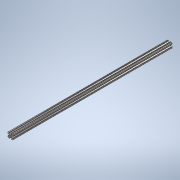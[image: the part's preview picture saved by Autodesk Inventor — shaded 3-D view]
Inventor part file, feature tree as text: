
AUTODESK INVENTOR PART (.ipt)
format: ipt  version: 2020 (Build 240168000, 168)  size: 244,224 bytes
history: native  units: in
note: dims shown in document units (in); Inventor stores cm internally (conversion verified against a paired STEP export)
features: extrude x1, sketch x1
ambient origin geometry x8: Origin, YZ Plane, XZ Plane, XY Plane, X Axis, Y Axis, Z Axis, Center Point
bodies: Solid1 (feature_tree)
feature tree (2):
  extrude  "Extrusion1"  [1 undecoded]
  sketch  "Sketch1"  dims[d0=31.0in d1=0.0in]
note: 1 required parameter value undecoded (feature->parameter linkage not recoverable at this tier; creation-order binding heuristic only, values carry confidence <= 0.55)
